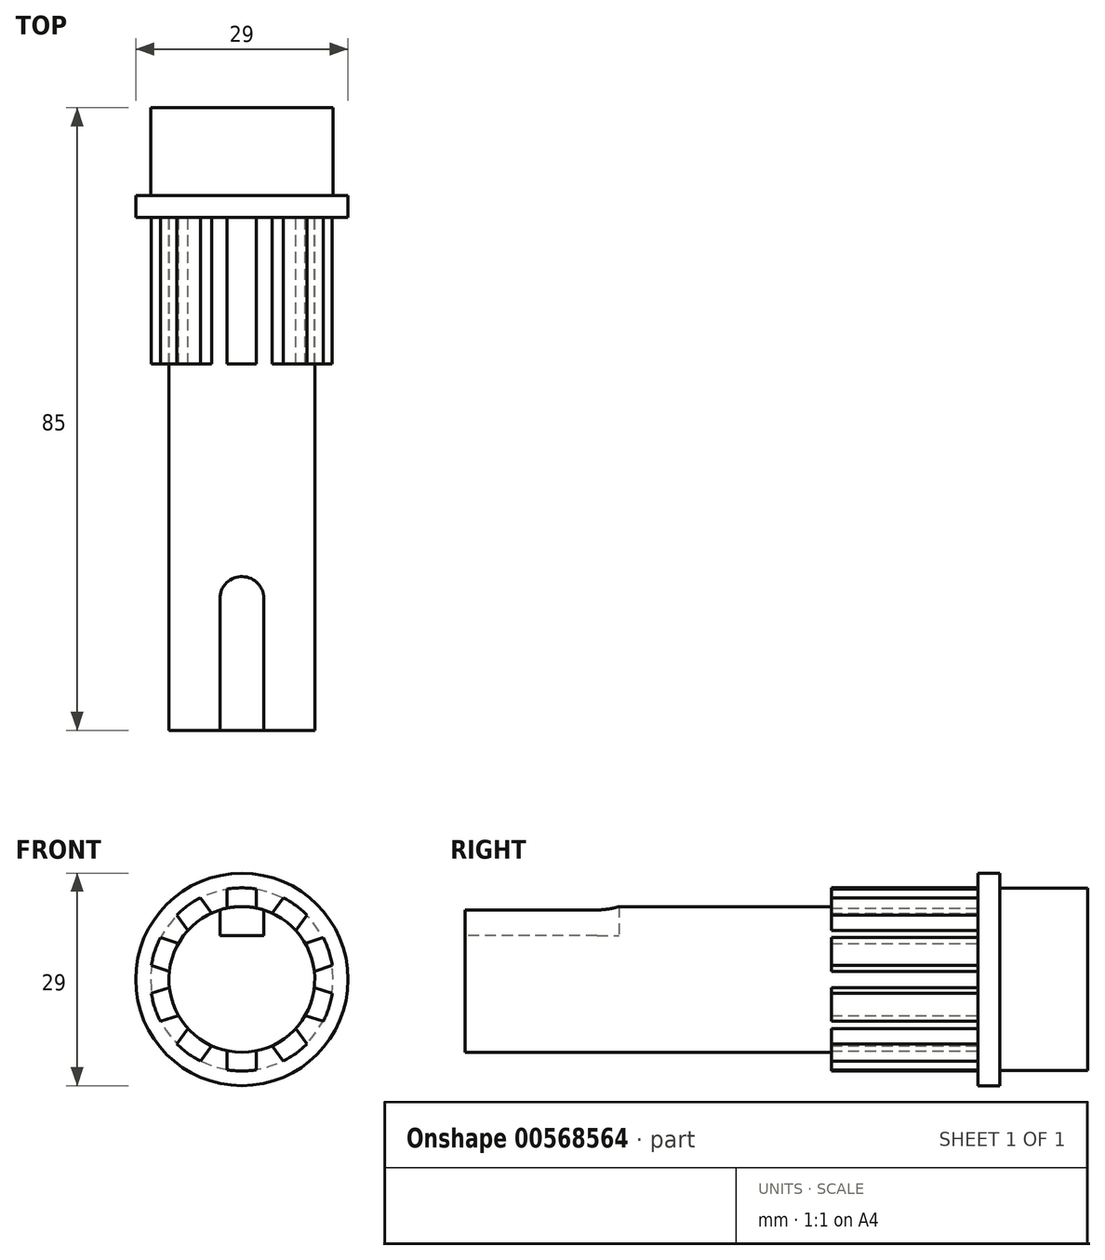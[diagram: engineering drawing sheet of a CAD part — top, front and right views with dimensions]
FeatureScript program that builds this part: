
annotation { "Feature Type Name" : "Feature", "Feature Type Description" : "" }
export const myFeature = defineFeature(function(context is Context, id is Id, definition is map)
    precondition{}
    {
        {
            var Q0;
            Q0=qCreatedBy(makeId("Front.planeOp"),FACE);
            var sketch = newSketch(context, id + "F0", { "sketchPlane" : qUnion([Q0])});
            skCircle(sketch, "E0", {"center": v(0, 0) * mm, "radius": 12.45 * mm});
            skSolve(sketch);
        }
        {
            var Q0;
            Q0=makeQuery(id+"F0.imprint","IMPRINT",FACE,{"disambiguationData":[TD([[makeQuery(id+"F0.imprint","IMPRINT",EDGE,{"derivedFrom":sQuery(id+"F0.wireOp",EDGE,"E0")}),1.0]])]});
            extrude(context, id + "F1", {"entities" : qUnion([Q0]), "oppositeDirection" : true, "depth" : 12 * mm, "offsetDistance" : 25 * mm});
        }
        {
            var Q0;
            Q0=qCreatedBy(makeId("Front.planeOp"),FACE);
            var sketch = newSketch(context, id + "F2", { "sketchPlane" : qUnion([Q0])});
            skCircle(sketch, "E1", {"center": v(0, 0) * mm, "radius": 14.5 * mm});
            skSolve(sketch);
        }
        {
            var Q0;
            Q0=makeQuery(id+"F2.imprint","IMPRINT",FACE,{"disambiguationData":[TD([[makeQuery(id+"F2.imprint","IMPRINT",EDGE,{"derivedFrom":sQuery(id+"F2.wireOp",EDGE,"E1")}),1.0]])]});
            extrude(context, id + "F3", {"entities" : qUnion([Q0]), "operationType" : NewBodyOperationType.ADD, "depth" : 3 * mm, "offsetDistance" : 25 * mm});
        }
        {
            var Q0;
            Q0=makeQuery(id+"F3.opExtrude","CAP_FACE",FACE,{"disambiguationData":[OSD([sQuery(id+"F2.wireOp",EDGE,"E1")])],"isStart":false});
            var sketch = newSketch(context, id + "F4", { "sketchPlane" : qUnion([Q0])});
            skCircle(sketch, "E2", {"center": v(0, 0) * mm, "radius": 9.95 * mm});
            skSolve(sketch);
        }
        {
            var Q0;
            Q0=makeQuery(id+"F4.imprint","IMPRINT",FACE,{"disambiguationData":[TD([[makeQuery(id+"F4.imprint","IMPRINT",EDGE,{"derivedFrom":sQuery(id+"F4.wireOp",EDGE,"E2")}),1.0]])]});
            extrude(context, id + "F5", {"entities" : qUnion([Q0]), "operationType" : NewBodyOperationType.ADD, "depth" : 70 * mm, "offsetDistance" : 25 * mm});
        }
        {
            var Q0;
            Q0=qCreatedBy(makeId("Top.planeOp"),FACE);
            cPlane(context, id + "F6", {"entities" : qUnion([Q0]), "cplaneType" : CPlaneType.OFFSET, "offset" : 6 * mm, "width" : 150 * mm, "height" : 150 * mm});
        }
        {
            var Q0;
            Q0=qCreatedBy(id+"F6.planeOp",FACE);
            var sketch = newSketch(context, id + "F7", { "sketchPlane" : qUnion([Q0])});
            skLineSegment(sketch, "E3.top", {"start": v(-3, -107.72) * mm, "end": v(3, -107.72) * mm});
            skLineSegment(sketch, "E3.left", {"start": v(-3, -55) * mm, "end": v(-3, -107.72) * mm});
            skLineSegment(sketch, "E3.right", {"start": v(3, -55) * mm, "end": v(3, -107.72) * mm});
            skArc(sketch, "E4", {"start": v(3, -55) * mm, "mid": v(0, -52) * mm, "end": v(-3, -55) * mm});
            skSolve(sketch);
        }
        {
            var Q0;
            Q0 = qSketchRegion(id + "F7", true);
            extrude(context, id + "F8", {"entities" : qUnion([Q0]), "operationType" : NewBodyOperationType.REMOVE, "depth" : 12 * mm, "offsetDistance" : 25 * mm});
        }
        {
            var Q0;
            Q0=makeQuery(id+"F3.opExtrude","CAP_FACE",FACE,{"disambiguationData":[OSD([sQuery(id+"F2.wireOp",EDGE,"E1")])],"isStart":false});
            var sketch = newSketch(context, id + "F9", { "sketchPlane" : qUnion([Q0])});
            skArc(sketch, "E5", {"start": v(-2, -12.34) * mm, "mid": v(0, -12.5) * mm, "end": v(2, -12.34) * mm});
            skLineSegment(sketch, "E6", {"start": v(-2, -12.34) * mm, "end": v(-2, -7.73) * mm});
            skLineSegment(sketch, "E7", {"start": v(-2, -7.73) * mm, "end": v(2, -7.73) * mm});
            skLineSegment(sketch, "E8", {"start": v(2, -7.73) * mm, "end": v(2, -12.34) * mm});
            skLineSegment(sketch, "E9.1.0", {"start": v(5.63, -11.16) * mm, "end": v(2.92, -7.43) * mm});
            skArc(sketch, "E9.1.1", {"start": v(5.63, -11.16) * mm, "mid": v(7.35, -10.11) * mm, "end": v(8.87, -8.8) * mm});
            skLineSegment(sketch, "E9.1.2", {"start": v(6.16, -5.08) * mm, "end": v(8.87, -8.8) * mm});
            skLineSegment(sketch, "E9.2.0", {"start": v(11.12, -5.72) * mm, "end": v(6.73, -4.3) * mm});
            skArc(sketch, "E9.2.1", {"start": v(11.12, -5.72) * mm, "mid": v(11.89, -3.86) * mm, "end": v(12.35, -1.91) * mm});
            skLineSegment(sketch, "E9.2.2", {"start": v(7.97, -0.49) * mm, "end": v(12.35, -1.91) * mm});
            skLineSegment(sketch, "E9.3.0", {"start": v(12.35, 1.91) * mm, "end": v(7.97, 0.49) * mm});
            skArc(sketch, "E9.3.1", {"start": v(12.35, 1.91) * mm, "mid": v(11.89, 3.86) * mm, "end": v(11.12, 5.72) * mm});
            skLineSegment(sketch, "E9.3.2", {"start": v(6.73, 4.3) * mm, "end": v(11.12, 5.72) * mm});
            skLineSegment(sketch, "E9.4.0", {"start": v(8.87, 8.8) * mm, "end": v(6.16, 5.08) * mm});
            skArc(sketch, "E9.4.1", {"start": v(8.87, 8.8) * mm, "mid": v(7.35, 10.11) * mm, "end": v(5.63, 11.16) * mm});
            skLineSegment(sketch, "E9.4.2", {"start": v(2.92, 7.43) * mm, "end": v(5.63, 11.16) * mm});
            skLineSegment(sketch, "E9.5.0", {"start": v(2, 12.34) * mm, "end": v(2, 7.73) * mm});
            skArc(sketch, "E9.5.1", {"start": v(2, 12.34) * mm, "mid": v(0, 12.5) * mm, "end": v(-2, 12.34) * mm});
            skLineSegment(sketch, "E9.5.2", {"start": v(-2, 7.73) * mm, "end": v(-2, 12.34) * mm});
            skLineSegment(sketch, "E9.6.0", {"start": v(-5.63, 11.16) * mm, "end": v(-2.92, 7.43) * mm});
            skArc(sketch, "E9.6.1", {"start": v(-5.63, 11.16) * mm, "mid": v(-7.35, 10.11) * mm, "end": v(-8.87, 8.8) * mm});
            skLineSegment(sketch, "E9.6.2", {"start": v(-6.16, 5.08) * mm, "end": v(-8.87, 8.8) * mm});
            skLineSegment(sketch, "E9.7.0", {"start": v(-11.12, 5.72) * mm, "end": v(-6.73, 4.3) * mm});
            skArc(sketch, "E9.7.1", {"start": v(-11.12, 5.72) * mm, "mid": v(-11.89, 3.86) * mm, "end": v(-12.35, 1.91) * mm});
            skLineSegment(sketch, "E9.7.2", {"start": v(-7.97, 0.49) * mm, "end": v(-12.35, 1.91) * mm});
            skLineSegment(sketch, "E9.8.0", {"start": v(-12.35, -1.91) * mm, "end": v(-7.97, -0.49) * mm});
            skArc(sketch, "E9.8.1", {"start": v(-12.35, -1.91) * mm, "mid": v(-11.89, -3.86) * mm, "end": v(-11.12, -5.72) * mm});
            skLineSegment(sketch, "E9.8.2", {"start": v(-6.73, -4.3) * mm, "end": v(-11.12, -5.72) * mm});
            skLineSegment(sketch, "E9.9.0", {"start": v(-8.87, -8.8) * mm, "end": v(-6.16, -5.08) * mm});
            skArc(sketch, "E9.9.1", {"start": v(-8.87, -8.8) * mm, "mid": v(-7.35, -10.11) * mm, "end": v(-5.63, -11.16) * mm});
            skLineSegment(sketch, "E9.9.2", {"start": v(-2.92, -7.43) * mm, "end": v(-5.63, -11.16) * mm});
            skSolve(sketch);
        }
        {
            var Q0;
            {var subQ0=sQuery(id+"F9.wireOp",EDGE,"E9.6.1");Q0=makeQuery(id+"F9.imprint","IMPRINT",FACE,{"disambiguationData":[TD([[makeQuery(id+"F9.imprint","IMPRINT",EDGE,{"derivedFrom":subQ0}),1.0]])]});}
            var Q1;
            {var subQ0=sQuery(id+"F9.wireOp",EDGE,"E9.5.1");Q1=makeQuery(id+"F9.imprint","IMPRINT",FACE,{"disambiguationData":[TD([[makeQuery(id+"F9.imprint","IMPRINT",EDGE,{"derivedFrom":subQ0}),1.0]])]});}
            var Q2;
            {var subQ0=sQuery(id+"F9.wireOp",EDGE,"E9.4.1");Q2=makeQuery(id+"F9.imprint","IMPRINT",FACE,{"disambiguationData":[TD([[makeQuery(id+"F9.imprint","IMPRINT",EDGE,{"derivedFrom":subQ0}),1.0]])]});}
            var Q3;
            {var subQ0=sQuery(id+"F9.wireOp",EDGE,"E9.3.1");Q3=makeQuery(id+"F9.imprint","IMPRINT",FACE,{"disambiguationData":[TD([[makeQuery(id+"F9.imprint","IMPRINT",EDGE,{"derivedFrom":subQ0}),1.0]])]});}
            var Q4;
            {var subQ0=sQuery(id+"F9.wireOp",EDGE,"E9.2.1");Q4=makeQuery(id+"F9.imprint","IMPRINT",FACE,{"disambiguationData":[TD([[makeQuery(id+"F9.imprint","IMPRINT",EDGE,{"derivedFrom":subQ0}),1.0]])]});}
            var Q5;
            {var subQ0=sQuery(id+"F9.wireOp",EDGE,"E9.7.1");Q5=makeQuery(id+"F9.imprint","IMPRINT",FACE,{"disambiguationData":[TD([[makeQuery(id+"F9.imprint","IMPRINT",EDGE,{"derivedFrom":subQ0}),1.0]])]});}
            var Q6;
            {var subQ0=sQuery(id+"F9.wireOp",EDGE,"E9.8.1");Q6=makeQuery(id+"F9.imprint","IMPRINT",FACE,{"disambiguationData":[TD([[makeQuery(id+"F9.imprint","IMPRINT",EDGE,{"derivedFrom":subQ0}),1.0]])]});}
            var Q7;
            {var subQ0=sQuery(id+"F9.wireOp",EDGE,"E9.9.1");Q7=makeQuery(id+"F9.imprint","IMPRINT",FACE,{"disambiguationData":[TD([[makeQuery(id+"F9.imprint","IMPRINT",EDGE,{"derivedFrom":subQ0}),1.0]])]});}
            var Q8;
            {var subQ0=sQuery(id+"F9.wireOp",EDGE,"E5");Q8=makeQuery(id+"F9.imprint","IMPRINT",FACE,{"disambiguationData":[TD([[makeQuery(id+"F9.imprint","IMPRINT",EDGE,{"derivedFrom":subQ0}),1.0]])]});}
            var Q9;
            {var subQ0=sQuery(id+"F9.wireOp",EDGE,"E9.1.1");Q9=makeQuery(id+"F9.imprint","IMPRINT",FACE,{"disambiguationData":[TD([[makeQuery(id+"F9.imprint","IMPRINT",EDGE,{"derivedFrom":subQ0}),1.0]])]});}
            extrude(context, id + "F10", {"entities" : qUnion([Q0, Q1, Q2, Q3, Q4, Q5, Q6, Q7, Q8, Q9]), "operationType" : NewBodyOperationType.ADD, "depth" : 20 * mm, "offsetDistance" : 25 * mm});
        }
    });
